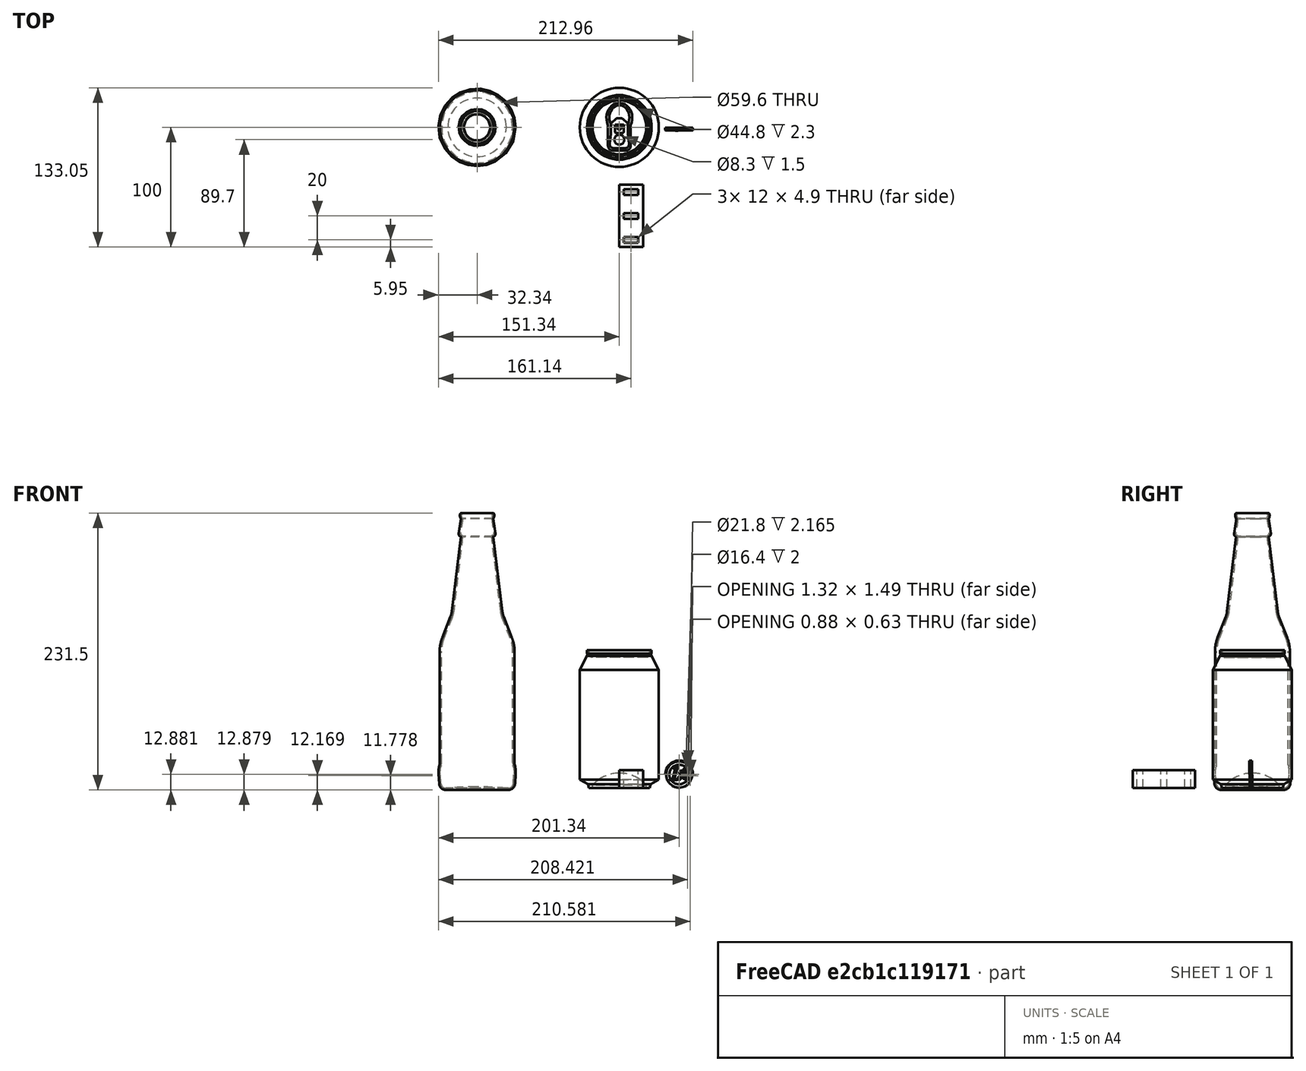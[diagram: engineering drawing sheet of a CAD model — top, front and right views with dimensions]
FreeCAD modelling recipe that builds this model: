
FCSTD DOCUMENT  (FreeCAD 0.20R29410 (Git))
Label: Portapendrives
License: All rights reserved
LicenseURL: http://en.wikipedia.org/wiki/All_rights_reserved
objects: Part::Box×4, Part::Feature×3, Part::MultiFuse×1, Part::Cut×1
note: 9 computed .brp shape members not serialized (recipe doc carries the construction recipe); baked Part::Feature solids carry a one-line shape summary decoded from their .brp

FEATURE [Part::Feature] Compound001  label="Euro-coin"
  Placement = pos=(50,99.808,10.9983) rot=(1,0,0;1.58825rad)
  shape: bbox 23.25 x 2.737 x 23.28 mm, 903 faces, 22 solids (baked)
FEATURE [Part::Feature] Thickness001  label="Bottle"
  Placement = pos=(-119,100,0) rot=(0,0,1;0rad)
  shape: bbox 71.75 x 74.3 x 235 mm, 40 faces (baked)
FEATURE [Part::Feature] Fusion001  label="Can"
  Placement = pos=(0,100,0) rot=(0,0,1;0rad)
  shape: bbox 66.1 x 66.1 x 115.2 mm, 53 faces (baked)
FEATURE [Part::Box] Box  label="Cubo"
  AttacherType = Attacher::AttachEngine3D
  Height = 15
  Length = 20
  Width = 52
FEATURE [Part::Box] Box001  label="Cubo001"
  AttacherType = Attacher::AttachEngine3D
  Height = 15
  Length = 12
  Placement = pos=(3.8,3.5,0) rot=(0,0,1;0rad)
  Width = 4.9
FEATURE [Part::Box] Box002  label="Cubo002"
  AttacherType = Attacher::AttachEngine3D
  Height = 15
  Length = 12
  Placement = pos=(3.8,23.5,0) rot=(0,0,1;0rad)
  Width = 4.9
FEATURE [Part::Box] Box003  label="Cubo003"
  AttacherType = Attacher::AttachEngine3D
  Height = 15
  Length = 12
  Placement = pos=(3.8,43.5,0) rot=(0,0,1;0rad)
  Width = 4.9
FEATURE [Part::MultiFuse] Fusion
  Shapes = -> [Box001,Box002,Box003]
FEATURE [Part::Cut] Cut
  Base = -> Box
  Tool = -> Fusion
